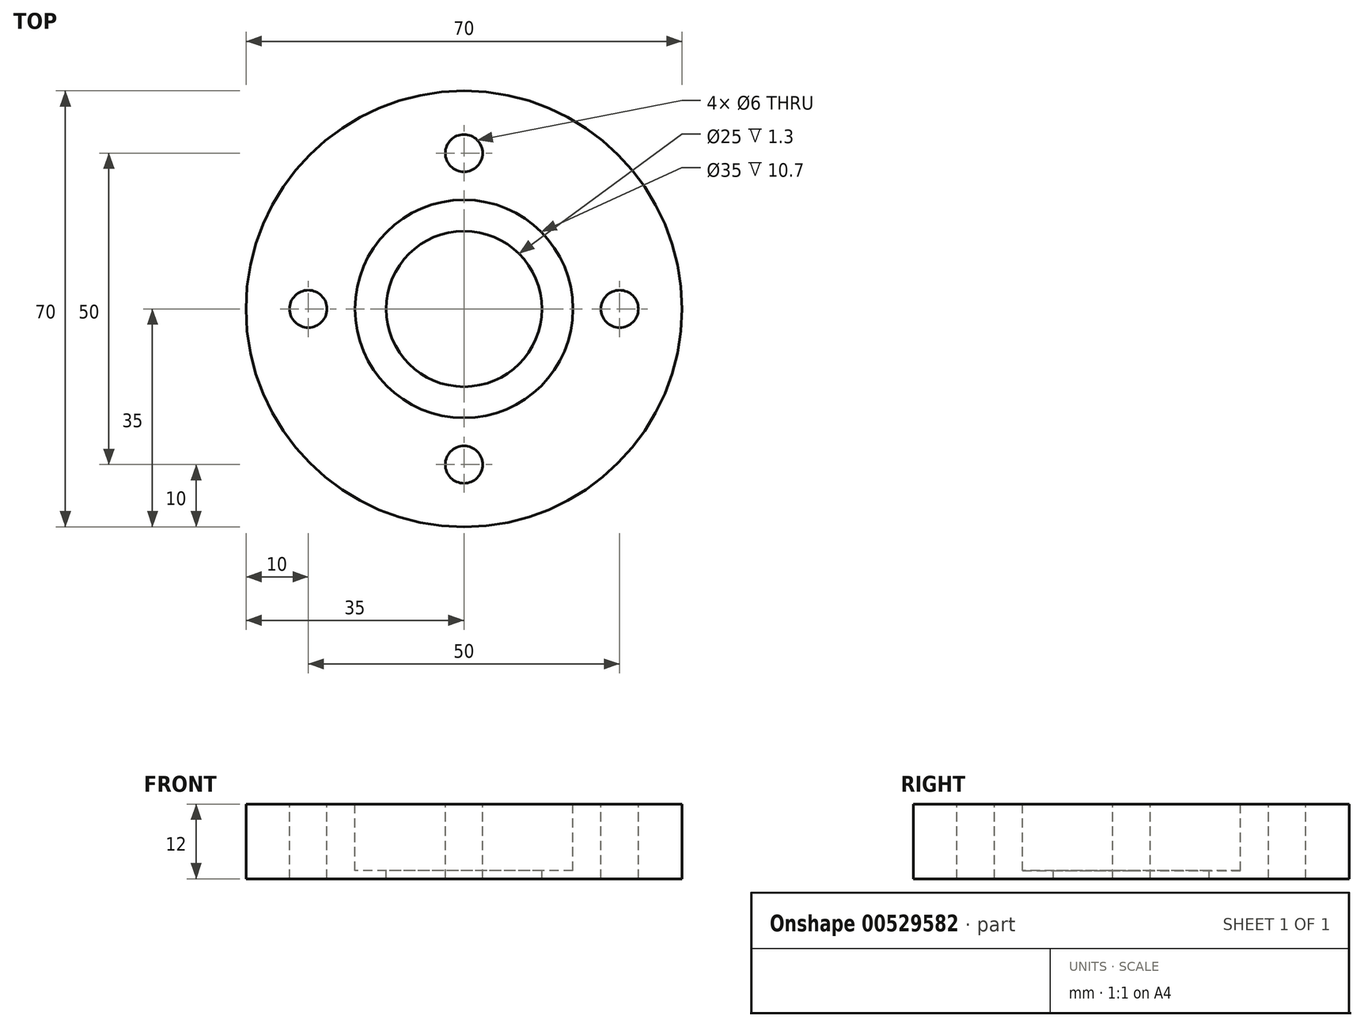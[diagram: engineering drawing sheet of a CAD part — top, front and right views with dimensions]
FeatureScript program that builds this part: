
annotation { "Feature Type Name" : "Feature", "Feature Type Description" : "" }
export const myFeature = defineFeature(function(context is Context, id is Id, definition is map)
    precondition{}
    {
        {
            var Q0;
            Q0=qCreatedBy(makeId("Top.planeOp"),FACE);
            var sketch = newSketch(context, id + "F0", { "sketchPlane" : qUnion([Q0])});
            skCircle(sketch, "E0", {"center": v(0, 0) * mm, "radius": 35 * mm});
            skSolve(sketch);
        }
        {
            var Q0;
            Q0 = qSketchRegion(id + "F0", true);
            extrude(context, id + "F1", {"entities" : qUnion([Q0]), "depth" : 12 * mm, "offsetDistance" : 25 * mm});
        }
        {
            var Q0;
            Q0=makeQuery(id+"F1.opExtrude","CAP_FACE",FACE,{"disambiguationData":[OSD([sQuery(id+"F0.wireOp",EDGE,"E0")])],"isStart":false});
            var sketch = newSketch(context, id + "F2", { "sketchPlane" : qUnion([Q0])});
            skCircle(sketch, "E1", {"center": v(0, 0) * mm, "radius": 12.5 * mm});
            skSolve(sketch);
        }
        {
            var Q0;
            Q0 = qSketchRegion(id + "F2", true);
            extrude(context, id + "F3", {"entities" : qUnion([Q0]), "operationType" : NewBodyOperationType.REMOVE, "oppositeDirection" : true, "depth" : 25 * mm, "offsetDistance" : 25 * mm});
        }
        {
            var Q0;
            Q0=makeQuery(id+"F1.opExtrude","CAP_FACE",FACE,{"disambiguationData":[OSD([sQuery(id+"F0.wireOp",EDGE,"E0")])],"isStart":false});
            var sketch = newSketch(context, id + "F4", { "sketchPlane" : qUnion([Q0])});
            skCircle(sketch, "E2", {"center": v(0, 0) * mm, "radius": 17.5 * mm});
            skSolve(sketch);
        }
        {
            var Q0;
            Q0 = qSketchRegion(id + "F4", true);
            extrude(context, id + "F5", {"entities" : qUnion([Q0]), "operationType" : NewBodyOperationType.REMOVE, "oppositeDirection" : true, "depth" : 10.7 * mm, "offsetDistance" : 25 * mm});
        }
        {
            var Q0;
            Q0=makeQuery(id+"F1.opExtrude","CAP_FACE",FACE,{"disambiguationData":[OSD([sQuery(id+"F0.wireOp",EDGE,"E0")])],"isStart":false});
            var sketch = newSketch(context, id + "F6", { "sketchPlane" : qUnion([Q0])});
            skCircle(sketch, "E3", {"center": v(-25, 0) * mm, "radius": 3 * mm});
            skCircle(sketch, "E4.1.0", {"center": v(0, -25) * mm, "radius": 3 * mm});
            skCircle(sketch, "E4.2.0", {"center": v(25, 0) * mm, "radius": 3 * mm});
            skCircle(sketch, "E4.3.0", {"center": v(0, 25) * mm, "radius": 3 * mm});
            skPoint(sketch, "E4.center", {"position": v(0, 0) * mm});
            skSolve(sketch);
        }
        {
            var Q0;
            Q0=makeQuery(id+"F6.imprint","IMPRINT",FACE,{"disambiguationData":[TD([[makeQuery(id+"F6.imprint","IMPRINT",EDGE,{"derivedFrom":sQuery(id+"F6.wireOp",EDGE,"E3")}),1.0]])]});
            var Q1;
            Q1=makeQuery(id+"F6.imprint","IMPRINT",FACE,{"disambiguationData":[TD([[makeQuery(id+"F6.imprint","IMPRINT",EDGE,{"derivedFrom":sQuery(id+"F6.wireOp",EDGE,"E4.3.0")}),1.0]])]});
            var Q2;
            Q2=makeQuery(id+"F6.imprint","IMPRINT",FACE,{"disambiguationData":[TD([[makeQuery(id+"F6.imprint","IMPRINT",EDGE,{"derivedFrom":sQuery(id+"F6.wireOp",EDGE,"E4.2.0")}),1.0]])]});
            var Q3;
            Q3=makeQuery(id+"F6.imprint","IMPRINT",FACE,{"disambiguationData":[TD([[makeQuery(id+"F6.imprint","IMPRINT",EDGE,{"derivedFrom":sQuery(id+"F6.wireOp",EDGE,"E4.1.0")}),1.0]])]});
            extrude(context, id + "F7", {"entities" : qUnion([Q0, Q1, Q2, Q3]), "operationType" : NewBodyOperationType.REMOVE, "oppositeDirection" : true, "depth" : 25 * mm, "offsetDistance" : 25 * mm});
        }
    });
